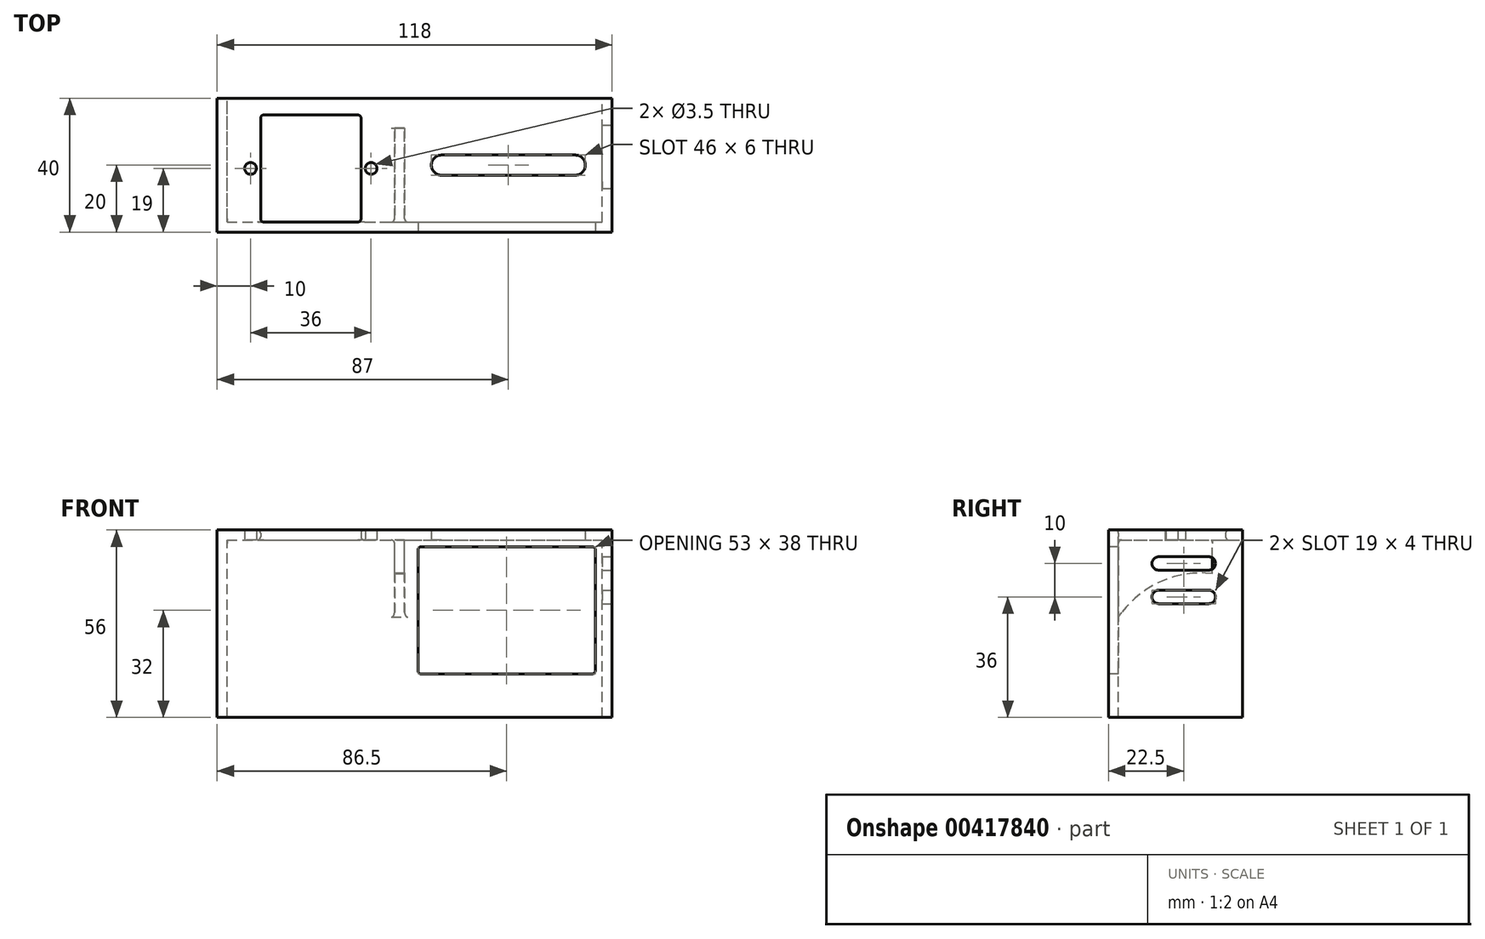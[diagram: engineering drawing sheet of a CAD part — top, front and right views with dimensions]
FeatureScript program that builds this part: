
annotation { "Feature Type Name" : "Feature", "Feature Type Description" : "" }
export const myFeature = defineFeature(function(context is Context, id is Id, definition is map)
    precondition{}
    {
        {
            var Q0;
            Q0=qCreatedBy(makeId("Top.planeOp"),FACE);
            var sketch = newSketch(context, id + "F0", { "sketchPlane" : qUnion([Q0])});
            skLineSegment(sketch, "E0.bottom", {"start": v(-59, -20) * mm, "end": v(59, -20) * mm});
            skLineSegment(sketch, "E0.top", {"start": v(-59, 20) * mm, "end": v(59, 20) * mm});
            skLineSegment(sketch, "E0.left", {"start": v(-59, -20) * mm, "end": v(-59, 20) * mm});
            skLineSegment(sketch, "E0.right", {"start": v(59, -20) * mm, "end": v(59, 20) * mm});
            skCircle(sketch, "E1", {"center": v(-49, -1) * mm, "radius": 1.75 * mm});
            skCircle(sketch, "E2", {"center": v(-13, -1) * mm, "radius": 1.75 * mm});
            skLineSegment(sketch, "E3.bottom", {"start": v(-46, -17) * mm, "end": v(-16, -17) * mm});
            skLineSegment(sketch, "E3.top", {"start": v(-46, 15) * mm, "end": v(-16, 15) * mm});
            skLineSegment(sketch, "E3.left", {"start": v(-46, -17) * mm, "end": v(-46, 15) * mm});
            skLineSegment(sketch, "E3.right", {"start": v(-16, -17) * mm, "end": v(-16, 15) * mm});
            skArc(sketch, "E4", {"start": v(8, 3) * mm, "mid": v(5, 0) * mm, "end": v(8, -3) * mm});
            skArc(sketch, "E5", {"start": v(48, -3) * mm, "mid": v(51, 0) * mm, "end": v(48, 3) * mm});
            skLineSegment(sketch, "E6", {"start": v(8, 3) * mm, "end": v(48, 3) * mm});
            skLineSegment(sketch, "E7", {"start": v(8, -3) * mm, "end": v(48, -3) * mm});
            skSolve(sketch);
        }
        {
            var Q0;
            Q0=makeQuery(id+"F0.imprint","IMPRINT",FACE,{"disambiguationData":[TD([[makeQuery(id+"F0.imprint","IMPRINT",EDGE,{"derivedFrom":sQuery(id+"F0.wireOp",EDGE,"E0.bottom")}),1.0]])]});
            extrude(context, id + "F1", {"entities" : qUnion([Q0]), "depth" : 3 * mm});
        }
        {
            var Q0;
            Q0=makeQuery(id+"F1.opExtrude","CAP_FACE",FACE,{"disambiguationData":[OSD([sQuery(id+"F0.wireOp",EDGE,"E0.bottom"),sQuery(id+"F0.wireOp",EDGE,"E0.top"),sQuery(id+"F0.wireOp",EDGE,"E0.left"),sQuery(id+"F0.wireOp",EDGE,"E0.right"),sQuery(id+"F0.wireOp",EDGE,"E1"),sQuery(id+"F0.wireOp",EDGE,"E2"),sQuery(id+"F0.wireOp",EDGE,"E3.bottom"),sQuery(id+"F0.wireOp",EDGE,"E3.top"),sQuery(id+"F0.wireOp",EDGE,"E3.left"),sQuery(id+"F0.wireOp",EDGE,"E3.right")])],"isStart":true});
            var sketch = newSketch(context, id + "F2", { "sketchPlane" : qUnion([Q0])});
            skLineSegment(sketch, "E8.bottom", {"start": v(-59, 20) * mm, "end": v(59, 20) * mm});
            skLineSegment(sketch, "E8.top", {"start": v(-56, 17) * mm, "end": v(-6, 17) * mm});
            skLineSegment(sketch, "E8.left", {"start": v(-59, 20) * mm, "end": v(-59, 17) * mm});
            skLineSegment(sketch, "E8.right", {"start": v(59, 20) * mm, "end": v(59, 17) * mm});
            skLineSegment(sketch, "E9.bottom", {"start": v(-59, 20) * mm, "end": v(-56, 20) * mm});
            skLineSegment(sketch, "E9.top", {"start": v(-59, -20) * mm, "end": v(-56, -20) * mm});
            skLineSegment(sketch, "E9.left", {"start": v(-59, 20) * mm, "end": v(-59, -20) * mm});
            skLineSegment(sketch, "E9.right", {"start": v(-56, 17) * mm, "end": v(-56, -20) * mm});
            skLineSegment(sketch, "E10.bottom", {"start": v(59, 20) * mm, "end": v(56, 20) * mm});
            skLineSegment(sketch, "E10.top", {"start": v(59, -20) * mm, "end": v(56, -20) * mm});
            skLineSegment(sketch, "E10.left", {"start": v(59, 20) * mm, "end": v(59, -20) * mm});
            skLineSegment(sketch, "E10.right", {"start": v(56, 17) * mm, "end": v(56, -20) * mm});
            skLineSegment(sketch, "E11.top", {"start": v(-3, -11) * mm, "end": v(-6, -11) * mm});
            skLineSegment(sketch, "E11.left", {"start": v(-3, 17) * mm, "end": v(-3, -11) * mm});
            skLineSegment(sketch, "E11.right", {"start": v(-6, 17) * mm, "end": v(-6, -11) * mm});
            skLineSegment(sketch, "E12.trimOffspring", {"start": v(-3, 17) * mm, "end": v(56, 17) * mm});
            skSolve(sketch);
        }
        {
            var Q0;
            Q0=makeQuery(id+"F2.imprint","IMPRINT",FACE,{"disambiguationData":[TD([[makeQuery(id+"F2.imprint","IMPRINT",EDGE,{"derivedFrom":sQuery(id+"F2.wireOp",EDGE,"E8.bottom")}),-1.0]])]});
            extrude(context, id + "F3", {"entities" : qUnion([Q0]), "operationType" : NewBodyOperationType.ADD, "depth" : 53 * mm});
        }
        {
            var Q0;
            Q0=makeQuery(id+"F3.boolean.opBoolean","MERGE",FACE,{"derivedFrom":[makeQuery(id+"F1.opExtrude","SWEPT_FACE",FACE,{"disambiguationData":[OSD([sQuery(id+"F0.wireOp",EDGE,"E0.right")])]}),makeQuery(id+"F3.opExtrude","SWEPT_FACE",FACE,{"disambiguationData":[OSD([sQuery(id+"F2.wireOp",EDGE,"E10.left")])]})]});
            var sketch = newSketch(context, id + "F4", { "sketchPlane" : qUnion([Q0])});
            skArc(sketch, "E13", {"start": v(-5, -5) * mm, "mid": v(-7, -7) * mm, "end": v(-5, -9) * mm});
            skArc(sketch, "E14", {"start": v(10, -9) * mm, "mid": v(12, -7) * mm, "end": v(10, -5) * mm});
            skArc(sketch, "E15", {"start": v(-5, -15) * mm, "mid": v(-7, -17) * mm, "end": v(-5, -19) * mm});
            skArc(sketch, "E16", {"start": v(10, -19) * mm, "mid": v(12, -17) * mm, "end": v(10, -15) * mm});
            skLineSegment(sketch, "E17", {"start": v(-5, -5) * mm, "end": v(10, -5) * mm});
            skLineSegment(sketch, "E18", {"start": v(-5, -9) * mm, "end": v(10, -9) * mm});
            skLineSegment(sketch, "E19", {"start": v(-5, -15) * mm, "end": v(10, -15) * mm});
            skLineSegment(sketch, "E20", {"start": v(-5, -19) * mm, "end": v(10, -19) * mm});
            skSolve(sketch);
        }
        {
            var Q0;
            Q0=makeQuery(id+"F4.imprint","IMPRINT",FACE,{"disambiguationData":[TD([[makeQuery(id+"F4.imprint","IMPRINT",EDGE,{"derivedFrom":sQuery(id+"F4.wireOp",EDGE,"E13")}),1.0]])]});
            var Q1;
            Q1=makeQuery(id+"F4.imprint","IMPRINT",FACE,{"disambiguationData":[TD([[makeQuery(id+"F4.imprint","IMPRINT",EDGE,{"derivedFrom":sQuery(id+"F4.wireOp",EDGE,"E15")}),1.0]])]});
            extrude(context, id + "F5", {"entities" : qUnion([Q0, Q1]), "operationType" : NewBodyOperationType.REMOVE, "oppositeDirection" : true, "depth" : 4 * mm});
        }
        {
            var Q0;
            Q0=makeQuery(id+"F3.boolean.opBoolean","MERGE",FACE,{"derivedFrom":[makeQuery(id+"F1.opExtrude","SWEPT_FACE",FACE,{"disambiguationData":[OSD([sQuery(id+"F0.wireOp",EDGE,"E0.bottom")])]}),makeQuery(id+"F3.opExtrude","SWEPT_FACE",FACE,{"disambiguationData":[OSD([sQuery(id+"F2.wireOp",EDGE,"E8.bottom"),sQuery(id+"F2.wireOp",EDGE,"E9.bottom"),sQuery(id+"F2.wireOp",EDGE,"E10.bottom")])]})]});
            var sketch = newSketch(context, id + "F6", { "sketchPlane" : qUnion([Q0])});
            skLineSegment(sketch, "E21.bottom", {"start": v(1, -2) * mm, "end": v(54, -2) * mm});
            skLineSegment(sketch, "E21.top", {"start": v(1, -40) * mm, "end": v(54, -40) * mm});
            skLineSegment(sketch, "E21.left", {"start": v(1, -2) * mm, "end": v(1, -40) * mm});
            skLineSegment(sketch, "E21.right", {"start": v(54, -2) * mm, "end": v(54, -40) * mm});
            skSolve(sketch);
        }
        {
            var Q0;
            Q0=makeQuery(id+"F6.imprint","IMPRINT",FACE,{"disambiguationData":[TD([[makeQuery(id+"F6.imprint","IMPRINT",EDGE,{"derivedFrom":sQuery(id+"F6.wireOp",EDGE,"E21.bottom")}),-1.0]])]});
            extrude(context, id + "F7", {"entities" : qUnion([Q0]), "operationType" : NewBodyOperationType.REMOVE, "oppositeDirection" : true, "depth" : 3 * mm});
        }
        {
            var Q0;
            Q0=makeQuery(id+"F3.opExtrude","SWEPT_FACE",FACE,{"disambiguationData":[OSD([sQuery(id+"F2.wireOp",EDGE,"E11.left")])]});
            var sketch = newSketch(context, id + "F8", { "sketchPlane" : qUnion([Q0])});
            skLineSegment(sketch, "E22.bottom", {"start": v(11, -53) * mm, "end": v(-17, -53) * mm});
            skLineSegment(sketch, "E22.top", {"start": v(11, -23) * mm, "end": v(-17, -23) * mm, "construction": true});
            skLineSegment(sketch, "E22.left", {"start": v(11, -53) * mm, "end": v(11, -23) * mm});
            skLineSegment(sketch, "E22.right", {"start": v(-17, -53) * mm, "end": v(-17, -23) * mm});
            skLineSegment(sketch, "E23", {"start": v(11, -23) * mm, "end": v(11, -10) * mm});
            skArc(sketch, "E24", {"start": v(11, -10) * mm, "mid": v(-4.8, -12.62) * mm, "end": v(-17, -23) * mm});
            skSolve(sketch);
        }
        {
            var Q0;
            Q0=makeQuery(id+"F8.imprint","IMPRINT",FACE,{"disambiguationData":[TD([[makeQuery(id+"F8.imprint","IMPRINT",EDGE,{"derivedFrom":sQuery(id+"F8.wireOp",EDGE,"E22.bottom")}),1.0]])]});
            extrude(context, id + "F9", {"entities" : qUnion([Q0]), "operationType" : NewBodyOperationType.REMOVE, "oppositeDirection" : true, "depth" : 3 * mm});
        }
        {
            var Q0;
            Q0=makeQuery(id+"F3.opExtrude","CAP_EDGE",EDGE,{"disambiguationData":[OSD([sQuery(id+"F2.wireOp",EDGE,"E12.trimOffspring")])],"isStart":true});
            var Q1;
            {var subQ1=sQuery(id+"F2.wireOp",EDGE,"E8.top");var subQ2=sQuery(id+"F0.wireOp",EDGE,"E3.right");Q1=makeQuery(id+"F3.boolean.opBoolean","SPLIT",EDGE,{"disambiguationData":[TD([makeQuery(id+"F1.opExtrude","SWEPT_FACE",FACE,{"disambiguationData":[OSD([subQ2])]})])],"derivedFrom":makeQuery(id+"F3.opExtrude","CAP_EDGE",EDGE,{"disambiguationData":[OSD([subQ1])],"isStart":true})});}
            var Q2;
            {var subQ0=sQuery(id+"F0.wireOp",EDGE,"E3.left");var subQ2=sQuery(id+"F2.wireOp",EDGE,"E8.top");Q2=makeQuery(id+"F3.boolean.opBoolean","SPLIT",EDGE,{"disambiguationData":[TD([makeQuery(id+"F1.opExtrude","SWEPT_FACE",FACE,{"disambiguationData":[OSD([subQ0])]})])],"derivedFrom":makeQuery(id+"F3.opExtrude","CAP_EDGE",EDGE,{"disambiguationData":[OSD([subQ2])],"isStart":true})});}
            var Q3;
            Q3=makeQuery(id+"F7.boolean.opBoolean","COPY",EDGE,{"derivedFrom":makeQuery(id+"F7.opExtrude","CAP_EDGE",EDGE,{"disambiguationData":[OSD([sQuery(id+"F6.wireOp",EDGE,"E21.bottom")])],"isStart":false})});
            var Q4;
            Q4=makeQuery(id+"F7.boolean.opBoolean","COPY",EDGE,{"derivedFrom":makeQuery(id+"F7.opExtrude","CAP_EDGE",EDGE,{"disambiguationData":[OSD([sQuery(id+"F6.wireOp",EDGE,"E21.right")])],"isStart":true})});
            var Q5;
            Q5=makeQuery(id+"F7.boolean.opBoolean","COPY",EDGE,{"derivedFrom":makeQuery(id+"F7.opExtrude","CAP_EDGE",EDGE,{"disambiguationData":[OSD([sQuery(id+"F6.wireOp",EDGE,"E21.top")])],"isStart":true})});
            var Q6;
            Q6=makeQuery(id+"F7.boolean.opBoolean","COPY",EDGE,{"derivedFrom":makeQuery(id+"F7.opExtrude","CAP_EDGE",EDGE,{"disambiguationData":[OSD([sQuery(id+"F6.wireOp",EDGE,"E21.left")])],"isStart":true})});
            var Q7;
            Q7=makeQuery(id+"F7.boolean.opBoolean","COPY",EDGE,{"derivedFrom":makeQuery(id+"F7.opExtrude","CAP_EDGE",EDGE,{"disambiguationData":[OSD([sQuery(id+"F6.wireOp",EDGE,"E21.left")])],"isStart":false})});
            var Q8;
            Q8=makeQuery(id+"F7.boolean.opBoolean","COPY",EDGE,{"derivedFrom":makeQuery(id+"F7.opExtrude","CAP_EDGE",EDGE,{"disambiguationData":[OSD([sQuery(id+"F6.wireOp",EDGE,"E21.right")])],"isStart":false})});
            var Q9;
            Q9=makeQuery(id+"F7.boolean.opBoolean","COPY",EDGE,{"derivedFrom":makeQuery(id+"F7.opExtrude","CAP_EDGE",EDGE,{"disambiguationData":[OSD([sQuery(id+"F6.wireOp",EDGE,"E21.top")])],"isStart":false})});
            var Q10;
            Q10=makeQuery(id+"F1.opExtrude","CAP_EDGE",EDGE,{"disambiguationData":[OSD([sQuery(id+"F0.wireOp",EDGE,"E3.right")])],"isStart":false});
            var Q11;
            Q11=makeQuery(id+"F1.opExtrude","CAP_EDGE",EDGE,{"disambiguationData":[OSD([sQuery(id+"F0.wireOp",EDGE,"E3.bottom")])],"isStart":false});
            var Q12;
            Q12=makeQuery(id+"F1.opExtrude","CAP_EDGE",EDGE,{"disambiguationData":[OSD([sQuery(id+"F0.wireOp",EDGE,"E3.left")])],"isStart":false});
            var Q13;
            Q13=makeQuery(id+"F1.opExtrude","CAP_EDGE",EDGE,{"disambiguationData":[OSD([sQuery(id+"F0.wireOp",EDGE,"E3.top")])],"isStart":false});
            var Q14;
            Q14=makeQuery(id+"F1.opExtrude","CAP_EDGE",EDGE,{"disambiguationData":[OSD([sQuery(id+"F0.wireOp",EDGE,"E3.top")])],"isStart":true});
            var Q15;
            Q15=makeQuery(id+"F1.opExtrude","CAP_EDGE",EDGE,{"disambiguationData":[OSD([sQuery(id+"F0.wireOp",EDGE,"E3.right")])],"isStart":true});
            var Q16;
            Q16=makeQuery(id+"F1.opExtrude","CAP_EDGE",EDGE,{"disambiguationData":[OSD([sQuery(id+"F0.wireOp",EDGE,"E3.left")])],"isStart":true});
            var Q17;
            Q17=makeQuery(id+"F7.boolean.opBoolean","COPY",EDGE,{"derivedFrom":makeQuery(id+"F7.opExtrude","CAP_EDGE",EDGE,{"disambiguationData":[OSD([sQuery(id+"F6.wireOp",EDGE,"E21.bottom")])],"isStart":true})});
            var Q18;
            Q18=makeQuery(id+"F1.opExtrude","SWEPT_EDGE",EDGE,{"disambiguationData":[OSD([sQuery(id+"F0.wireOp",EDGE,"E3.top"),sQuery(id+"F0.wireOp",EDGE,"E3.right")])]});
            var Q19;
            Q19=makeQuery(id+"F1.opExtrude","SWEPT_EDGE",EDGE,{"disambiguationData":[OSD([sQuery(id+"F0.wireOp",EDGE,"E3.top"),sQuery(id+"F0.wireOp",EDGE,"E3.left")])]});
            var Q20;
            Q20=makeQuery(id+"F1.opExtrude","SWEPT_EDGE",EDGE,{"disambiguationData":[OSD([sQuery(id+"F0.wireOp",EDGE,"E3.bottom"),sQuery(id+"F0.wireOp",EDGE,"E3.left")])]});
            var Q21;
            Q21=makeQuery(id+"F1.opExtrude","SWEPT_EDGE",EDGE,{"disambiguationData":[OSD([sQuery(id+"F0.wireOp",EDGE,"E3.bottom"),sQuery(id+"F0.wireOp",EDGE,"E3.right")])]});
            var Q22;
            Q22=makeQuery(id+"F7.boolean.opBoolean","COPY",EDGE,{"derivedFrom":makeQuery(id+"F7.opExtrude","SWEPT_EDGE",EDGE,{"disambiguationData":[OSD([sQuery(id+"F6.wireOp",EDGE,"E21.bottom"),sQuery(id+"F6.wireOp",EDGE,"E21.right")])]})});
            var Q23;
            Q23=makeQuery(id+"F7.boolean.opBoolean","COPY",EDGE,{"derivedFrom":makeQuery(id+"F7.opExtrude","SWEPT_EDGE",EDGE,{"disambiguationData":[OSD([sQuery(id+"F6.wireOp",EDGE,"E21.top"),sQuery(id+"F6.wireOp",EDGE,"E21.right")])]})});
            var Q24;
            Q24=makeQuery(id+"F7.boolean.opBoolean","COPY",EDGE,{"derivedFrom":makeQuery(id+"F7.opExtrude","SWEPT_EDGE",EDGE,{"disambiguationData":[OSD([sQuery(id+"F6.wireOp",EDGE,"E21.top"),sQuery(id+"F6.wireOp",EDGE,"E21.left")])]})});
            var Q25;
            Q25=makeQuery(id+"F7.boolean.opBoolean","COPY",EDGE,{"derivedFrom":makeQuery(id+"F7.opExtrude","SWEPT_EDGE",EDGE,{"disambiguationData":[OSD([sQuery(id+"F6.wireOp",EDGE,"E21.bottom"),sQuery(id+"F6.wireOp",EDGE,"E21.left")])]})});
            var Q26;
            Q26=makeQuery(id+"F3.opExtrude","CAP_EDGE",EDGE,{"disambiguationData":[OSD([sQuery(id+"F2.wireOp",EDGE,"E11.left")])],"isStart":true});
            var Q27;
            Q27=makeQuery(id+"F3.opExtrude","CAP_EDGE",EDGE,{"disambiguationData":[OSD([sQuery(id+"F2.wireOp",EDGE,"E11.top")])],"isStart":true});
            var Q28;
            Q28=makeQuery(id+"F3.opExtrude","CAP_EDGE",EDGE,{"disambiguationData":[OSD([sQuery(id+"F2.wireOp",EDGE,"E11.right")])],"isStart":true});
            var Q29;
            Q29=makeQuery(id+"F3.opExtrude","SWEPT_EDGE",EDGE,{"disambiguationData":[OSD([sQuery(id+"F2.wireOp",EDGE,"E8.top"),sQuery(id+"F2.wireOp",EDGE,"E11.right")])]});
            var Q30;
            Q30=makeQuery(id+"F3.opExtrude","SWEPT_EDGE",EDGE,{"disambiguationData":[OSD([sQuery(id+"F2.wireOp",EDGE,"E11.left"),sQuery(id+"F2.wireOp",EDGE,"E12.trimOffspring")])]});
            var Q31;
            Q31=makeQuery(id+"F9.boolean.opBoolean","COPY",EDGE,{"derivedFrom":makeQuery(id+"F9.opExtrude","SWEPT_EDGE",EDGE,{"disambiguationData":[OSD([sQuery(id+"F2.wireOp",EDGE,"E11.top"),sQuery(id+"F2.wireOp",EDGE,"E11.left"),sQuery(id+"F8.wireOp",EDGE,"E23"),sQuery(id+"F8.wireOp",EDGE,"E24")])]})});
            fillet(context, id + "F10", {"entities" : qUnion([Q0, Q1, Q2, Q3, Q4, Q5, Q6, Q7, Q8, Q9, Q10, Q11, Q12, Q13, Q14, Q15, Q16, Q17, Q18, Q19, Q20, Q21, Q22, Q23, Q24, Q25, Q26, Q27, Q28, Q29, Q30, Q31]), "radius" : 1 * mm, "tangentPropagation" : true, "allowEdgeOverflow" : false});
        }
    });
